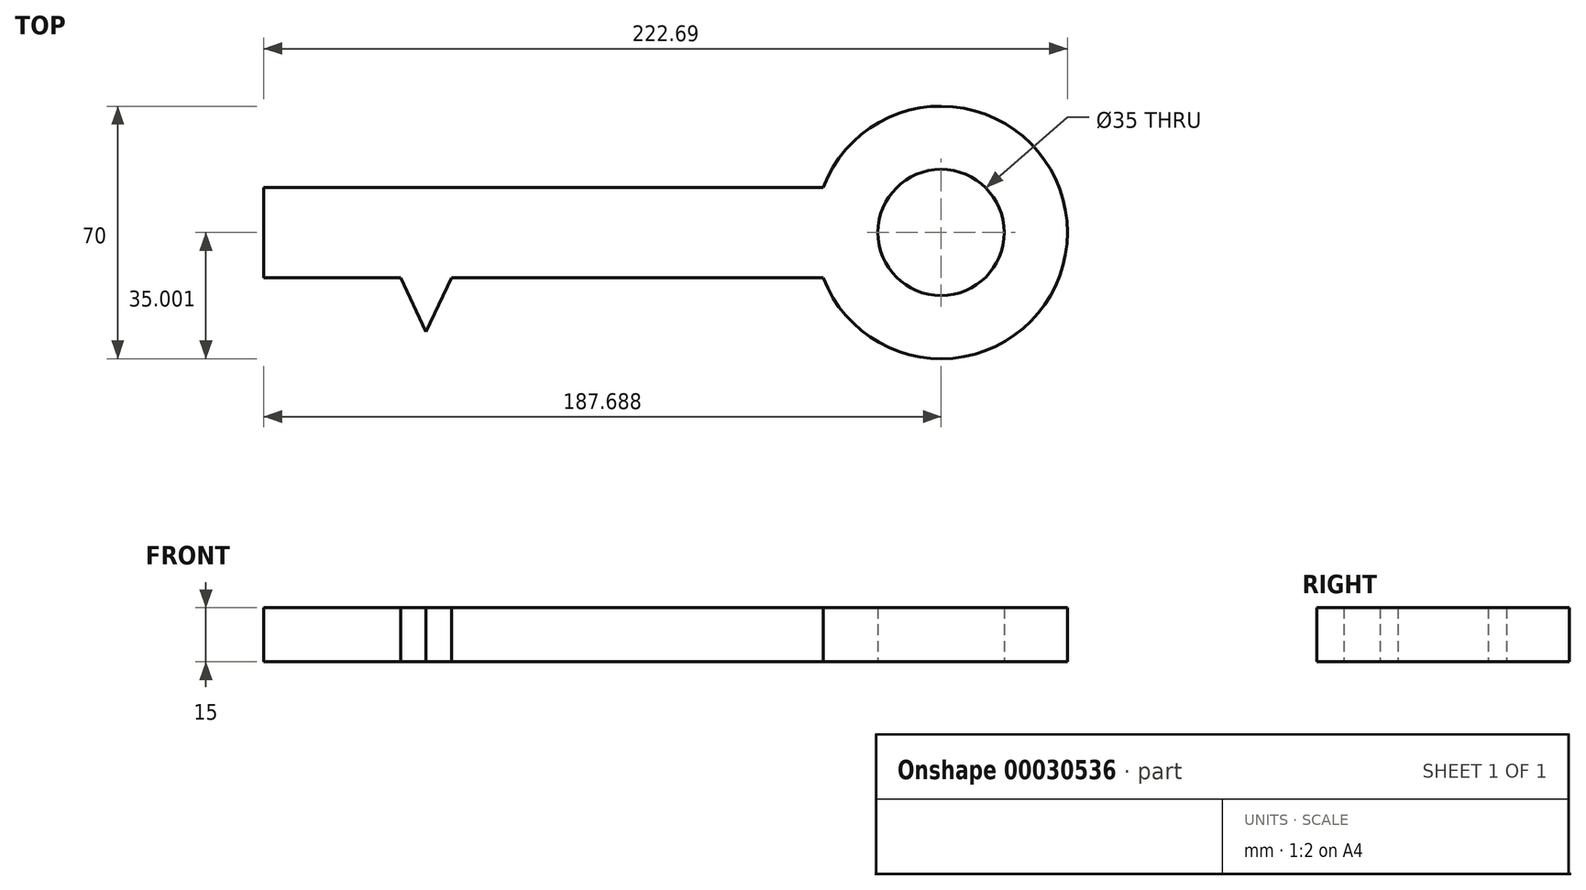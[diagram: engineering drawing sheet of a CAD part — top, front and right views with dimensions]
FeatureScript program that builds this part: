
annotation { "Feature Type Name" : "Feature", "Feature Type Description" : "" }
export const myFeature = defineFeature(function(context is Context, id is Id, definition is map)
    precondition{}
    {
        {
            var Q0;
            Q0=qCreatedBy(makeId("Top.planeOp"),FACE);
            var sketch = newSketch(context, id + "F0", { "sketchPlane" : qUnion([Q0])});
            skLineSegment(sketch, "E0.bottom", {"start": v(-124.25, 16.62) * mm, "end": v(30.75, 16.62) * mm});
            skLineSegment(sketch, "E0.top", {"start": v(-124.25, -8.38) * mm, "end": v(30.75, -8.38) * mm});
            skLineSegment(sketch, "E0.left", {"start": v(-124.25, 16.62) * mm, "end": v(-124.25, -8.38) * mm});
            skLineSegment(sketch, "E1.bottom", {"start": v(-124.25, -8.38) * mm, "end": v(-114.25, -8.38) * mm});
            skLineSegment(sketch, "E1.top", {"start": v(-124.25, -38.38) * mm, "end": v(-114.25, -38.38) * mm});
            skLineSegment(sketch, "E1.left", {"start": v(-124.25, -8.38) * mm, "end": v(-124.25, -38.38) * mm});
            skLineSegment(sketch, "E1.right", {"start": v(-114.25, -8.38) * mm, "end": v(-114.25, -38.38) * mm});
            skLineSegment(sketch, "E2.bottom", {"start": v(-104.25, -8.38) * mm, "end": v(-96.25, -8.38) * mm});
            skLineSegment(sketch, "E2.top", {"start": v(-104.25, -23.38) * mm, "end": v(-96.25, -23.38) * mm});
            skLineSegment(sketch, "E2.left", {"start": v(-104.25, -8.38) * mm, "end": v(-104.25, -23.38) * mm});
            skLineSegment(sketch, "E2.right", {"start": v(-96.25, -8.38) * mm, "end": v(-96.25, -23.38) * mm});
            skLineSegment(sketch, "E3", {"start": v(-86.25, -8.38) * mm, "end": v(-79.28, -23.38) * mm});
            skLineSegment(sketch, "E4", {"start": v(-79.28, -23.38) * mm, "end": v(-72.25, -8.38) * mm});
            skArc(sketch, "E5", {"start": v(30.75, -8.38) * mm, "mid": v(98.44, 4.12) * mm, "end": v(30.75, 16.62) * mm});
            skCircle(sketch, "E6", {"center": v(63.44, 4.12) * mm, "radius": 17.5 * mm});
            skLineSegment(sketch, "E7", {"start": v(-124.25, 4.12) * mm, "end": v(63.44, 4.12) * mm, "construction": true});
            skSolve(sketch);
        }
        {
            var Q0;
            Q0=makeQuery(id+"F0.imprint","IMPRINT",FACE,{"disambiguationData":[TD([[makeQuery(id+"F0.imprint","IMPRINT",EDGE,{"derivedFrom":sQuery(id+"F0.wireOp",EDGE,"E0.bottom")}),-1.0]])]});
            var Q1;
            Q1=makeQuery(id+"F0.imprint","IMPRINT",FACE,{"disambiguationData":[TD([[makeQuery(id+"F0.imprint","IMPRINT",EDGE,{"derivedFrom":sQuery(id+"F0.wireOp",EDGE,"E1.bottom")}),-1.0]])]});
            var Q2;
            Q2=makeQuery(id+"F0.imprint","IMPRINT",FACE,{"disambiguationData":[TD([[makeQuery(id+"F0.imprint","IMPRINT",EDGE,{"derivedFrom":sQuery(id+"F0.wireOp",EDGE,"E2.bottom")}),-1.0]])]});
            var Q3;
            {var subQ1=sQuery(id+"F0.wireOp",EDGE,"E3");Q3=makeQuery(id+"F0.imprint","IMPRINT",FACE,{"disambiguationData":[TD([[makeQuery(id+"F0.imprint","IMPRINT",EDGE,{"derivedFrom":subQ1}),1.0]])]});}
            extrude(context, id + "F1", {"entities" : qUnion([Q0, Q1, Q2, Q3]), "depth" : 15 * mm});
        }
    });
